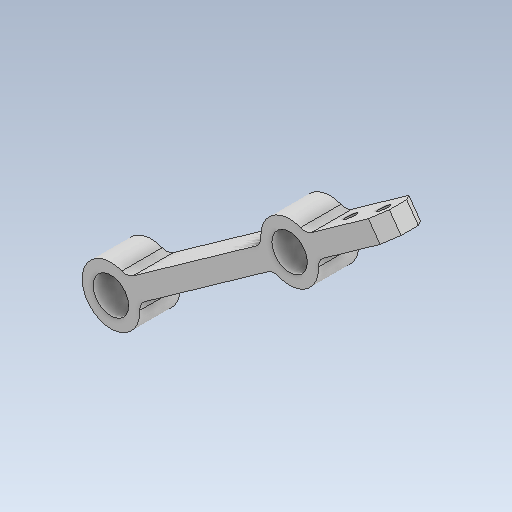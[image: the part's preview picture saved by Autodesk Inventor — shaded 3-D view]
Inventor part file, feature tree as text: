
AUTODESK INVENTOR PART (.ipt)
format: ipt  version: 2020 (Build 240168000, 168)  size: 128,000 bytes
history: native  units: mm
features: other x3, sketch x2
ambient origin geometry x8: Origin, YZ Plane, XZ Plane, XY Plane, X Axis, Y Axis, Z Axis, Center Point
bodies: Solid1 (feature_tree)
feature tree (5):
  other  "leg_link_1.ipt"
  other  "Solid1::leg_link_1.ipt"
  other  "TaggingFeature1"
  sketch  "Sketch1"  dims[d0=10.0mm]
  sketch  "Sketch2"
